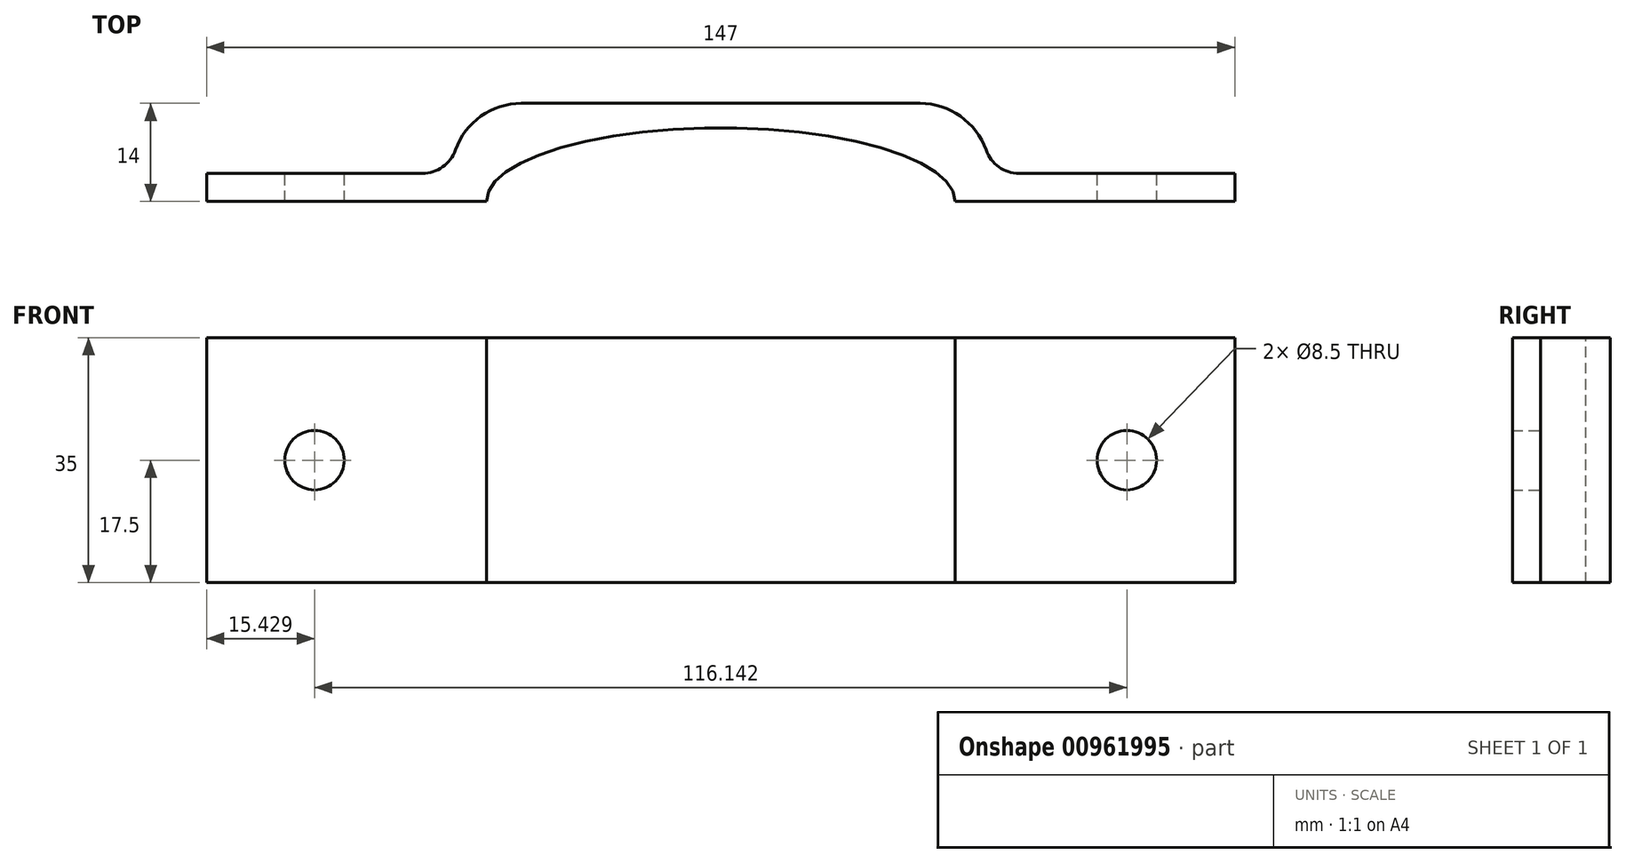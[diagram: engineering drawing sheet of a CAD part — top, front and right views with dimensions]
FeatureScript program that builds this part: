
annotation { "Feature Type Name" : "Feature", "Feature Type Description" : "" }
export const myFeature = defineFeature(function(context is Context, id is Id, definition is map)
    precondition{}
    {
        {
            var Q0;
            Q0=qCreatedBy(makeId("Top.planeOp"),FACE);
            var sketch = newSketch(context, id + "F0", { "sketchPlane" : qUnion([Q0])});
            skEllipticalArc(sketch, "E0", {});
            skLineSegment(sketch, "E1", {"start": v(0, 14) * mm, "end": v(38.5, 14) * mm});
            skLineSegment(sketch, "E2", {"start": v(38.5, 14) * mm, "end": v(38.5, 4) * mm});
            skLineSegment(sketch, "E3", {"start": v(38.5, 4) * mm, "end": v(73.5, 4) * mm});
            skLineSegment(sketch, "E4", {"start": v(73.5, 4) * mm, "end": v(73.5, 0) * mm});
            skLineSegment(sketch, "E5", {"start": v(73.5, 0) * mm, "end": v(33.5, 0) * mm});
            skPoint(sketch, "E6.endSnap0", {"position": v(0, 10.5) * mm});
            skLineSegment(sketch, "E7.MirrorCS", {"start": v(-73.5, 0) * mm, "end": v(-33.5, 0) * mm});
            skLineSegment(sketch, "E8.MirrorCS", {"start": v(-73.5, 4) * mm, "end": v(-73.5, 0) * mm});
            skLineSegment(sketch, "E9.MirrorCS", {"start": v(-38.5, 4) * mm, "end": v(-73.5, 4) * mm});
            skLineSegment(sketch, "E10.MirrorCS", {"start": v(0, 14) * mm, "end": v(-38.5, 14) * mm});
            skLineSegment(sketch, "E11.MirrorCS", {"start": v(-38.5, 14) * mm, "end": v(-38.5, 4) * mm});
            const initialGuessF0  = {"E0": [0, 0, -1, 0, 0.0335, 0.0105, 3.141592653589793, 0]};
            skSetInitialGuess(sketch, initialGuessF0);
            skSolve(sketch);
        }
        {
            var Q0;
            Q0=makeQuery(id+"F0.imprint","IMPRINT",FACE,{"disambiguationData":[TD([[makeQuery(id+"F0.imprint","IMPRINT",EDGE,{"derivedFrom":sQuery(id+"F0.wireOp",EDGE,"E0")}),-1.0]])]});
            extrude(context, id + "F1", {"entities" : qUnion([Q0]), "depth" : 35 * mm, "offsetDistance" : 25 * mm});
        }
        {
            var Q0;
            Q0=makeQuery(id+"F1.opExtrude","SWEPT_EDGE",EDGE,{"disambiguationData":[OSD([sQuery(id+"F0.wireOp",EDGE,"E1"),sQuery(id+"F0.wireOp",EDGE,"E2")])]});
            var Q1;
            Q1=makeQuery(id+"F1.opExtrude","SWEPT_EDGE",EDGE,{"disambiguationData":[OSD([sQuery(id+"F0.wireOp",EDGE,"zTefYsMn-vugA-d7js-uxrd-Z7QwKtC6hK2F"),sQuery(id+"F0.wireOp",EDGE,"E1")])]});
            var Q2;
            Q2=makeQuery(id+"F1.opExtrude","SWEPT_EDGE",EDGE,{"disambiguationData":[OSD([sQuery(id+"F0.wireOp",EDGE,"E10.MirrorCS"),sQuery(id+"F0.wireOp",EDGE,"E11.MirrorCS")])]});
            fillet(context, id + "F2", {"entities" : qUnion([Q0, Q1, Q2]), "radius" : 10 * mm, "tangentPropagation" : true, "allowEdgeOverflow" : false});
        }
        {
            var Q0;
            Q0=makeQuery(id+"F2.opFillet","BLEND_EDGE",EDGE,{"blendedFrom":[makeQuery(id+"F1.opExtrude","SWEPT_EDGE",EDGE,{"disambiguationData":[OSD([sQuery(id+"F0.wireOp",EDGE,"E1"),sQuery(id+"F0.wireOp",EDGE,"E2")])]}),makeQuery(id+"F1.opExtrude","SWEPT_FACE",FACE,{"disambiguationData":[OSD([sQuery(id+"F0.wireOp",EDGE,"E3")])]})],"blendedInto":[makeQuery(id+"F1.opExtrude","SWEPT_FACE",FACE,{"disambiguationData":[OSD([sQuery(id+"F0.wireOp",EDGE,"E3")])]})]});
            var Q1;
            Q1=makeQuery(id+"F2.opFillet","BLEND_EDGE",EDGE,{"blendedFrom":[makeQuery(id+"F1.opExtrude","SWEPT_EDGE",EDGE,{"disambiguationData":[OSD([sQuery(id+"F0.wireOp",EDGE,"E10.MirrorCS"),sQuery(id+"F0.wireOp",EDGE,"E11.MirrorCS")])]}),makeQuery(id+"F1.opExtrude","SWEPT_FACE",FACE,{"disambiguationData":[OSD([sQuery(id+"F0.wireOp",EDGE,"E9.MirrorCS")])]})],"blendedInto":[makeQuery(id+"F1.opExtrude","SWEPT_FACE",FACE,{"disambiguationData":[OSD([sQuery(id+"F0.wireOp",EDGE,"E9.MirrorCS")])]})]});
            fillet(context, id + "F3", {"entities" : qUnion([Q0, Q1]), "radius" : 5 * mm, "tangentPropagation" : true, "allowEdgeOverflow" : false});
        }
        {
            var Q0;
            Q0=makeQuery(id+"F1.opExtrude","SWEPT_FACE",FACE,{"disambiguationData":[OSD([sQuery(id+"F0.wireOp",EDGE,"E3")])]});
            var sketch = newSketch(context, id + "F4", { "sketchPlane" : qUnion([Q0])});
            skCircle(sketch, "E12", {"center": v(-58.07, 17.5) * mm, "radius": 4.25 * mm});
            skPoint(sketch, "E12.centerSnap0", {"position": v(-73.5, 17.5) * mm});
            skPoint(sketch, "E12.centerSnap1", {"position": v(-58.07, 35) * mm});
            skCircle(sketch, "E13.MirrorC", {"center": v(58.07, 17.5) * mm, "radius": 4.25 * mm});
            skSolve(sketch);
        }
        {
            var Q0;
            Q0 = qSketchRegion(id + "F4", true);
            extrude(context, id + "F5", {"entities" : qUnion([Q0]), "operationType" : NewBodyOperationType.REMOVE, "oppositeDirection" : true, "depth" : 25 * mm, "offsetDistance" : 25 * mm});
        }
    });
